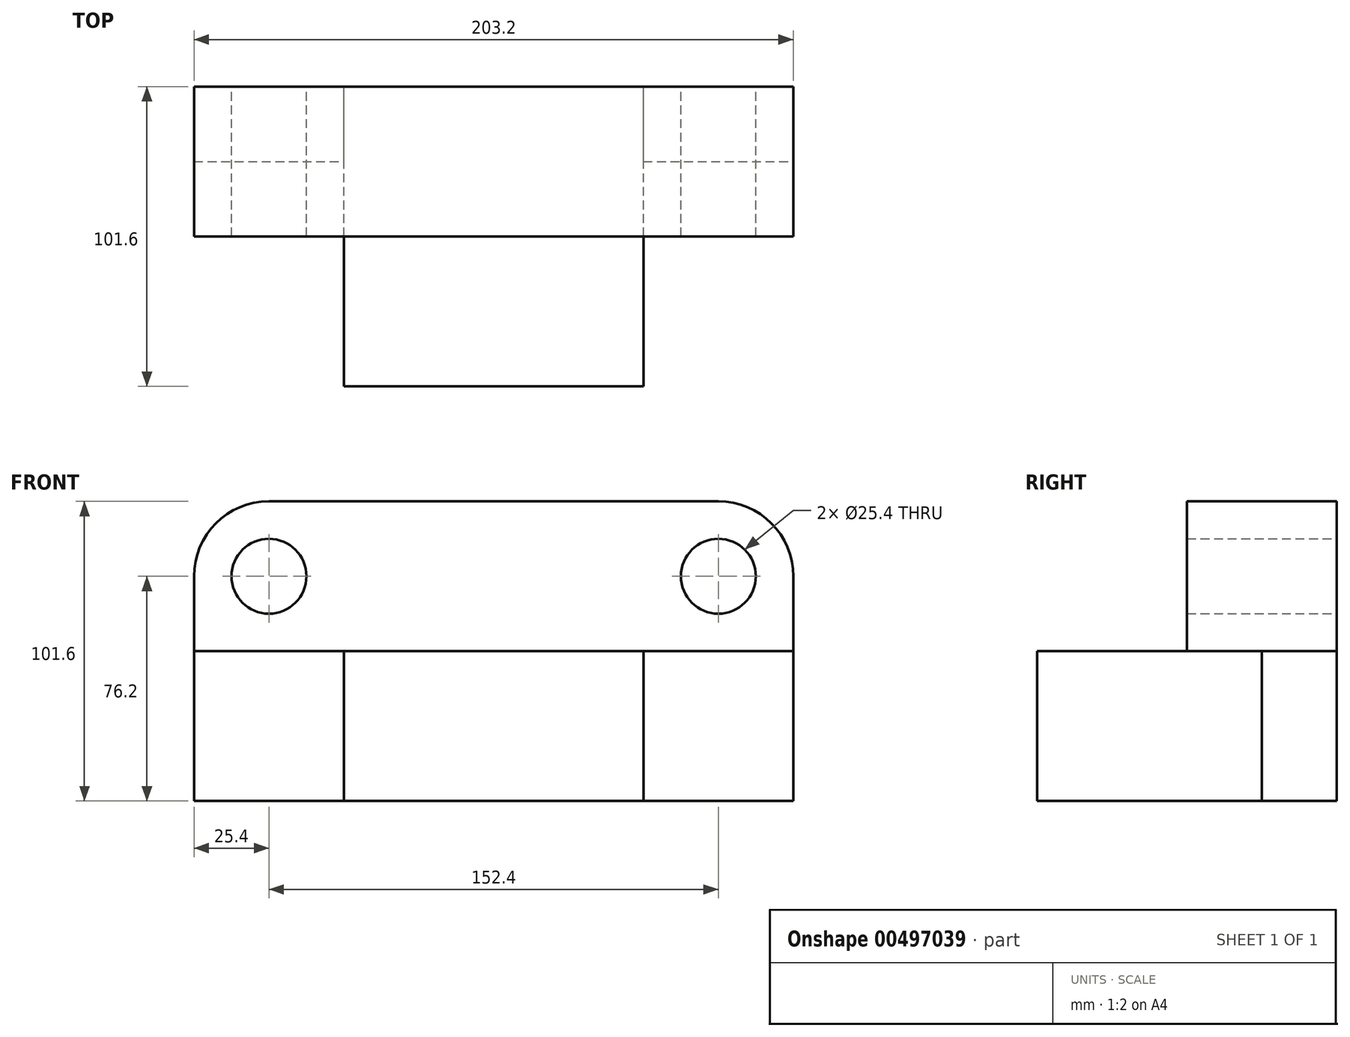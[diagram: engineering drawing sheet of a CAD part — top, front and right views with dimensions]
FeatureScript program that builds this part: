
annotation { "Feature Type Name" : "Feature", "Feature Type Description" : "" }
export const myFeature = defineFeature(function(context is Context, id is Id, definition is map)
    precondition{}
    {
        {
            var Q0;
            Q0=qCreatedBy(makeId("Front.planeOp"),FACE);
            var sketch = newSketch(context, id + "F0", { "sketchPlane" : qUnion([Q0])});
            skLineSegment(sketch, "E0.top", {"start": v(0, 50.8) * mm, "end": v(203.2, 50.8) * mm});
            skLineSegment(sketch, "E1.bottom", {"start": v(0, 0) * mm, "end": v(50.8, 0) * mm});
            skLineSegment(sketch, "E1.left", {"start": v(0, 0) * mm, "end": v(0, 50.8) * mm});
            skLineSegment(sketch, "E1.right", {"start": v(50.8, 0) * mm, "end": v(50.8, 50.8) * mm});
            skLineSegment(sketch, "E2.bottom", {"start": v(50.8, 0) * mm, "end": v(152.4, 0) * mm});
            skLineSegment(sketch, "E2.top", {"start": v(50.8, 50.8) * mm, "end": v(152.4, 50.8) * mm});
            skLineSegment(sketch, "E2.right", {"start": v(152.4, 0) * mm, "end": v(152.4, 50.8) * mm});
            skLineSegment(sketch, "E3.bottom", {"start": v(152.4, 0) * mm, "end": v(203.2, 0) * mm});
            skLineSegment(sketch, "E3.top", {"start": v(152.4, 50.8) * mm, "end": v(203.2, 50.8) * mm});
            skLineSegment(sketch, "E4", {"start": v(203.2, 0) * mm, "end": v(203.2, 50.8) * mm});
            skLineSegment(sketch, "E5.top", {"start": v(0, 101.6) * mm, "end": v(203.2, 101.6) * mm});
            skLineSegment(sketch, "E5.left", {"start": v(0, 50.8) * mm, "end": v(0, 101.6) * mm});
            skLineSegment(sketch, "E5.right", {"start": v(203.2, 50.8) * mm, "end": v(203.2, 101.6) * mm});
            skLineSegment(sketch, "E6", {"start": v(203.2, 101.6) * mm, "end": v(203.2, 76.2) * mm});
            skCircle(sketch, "E7", {"center": v(25.4, 76.2) * mm, "radius": 12.7 * mm});
            skCircle(sketch, "E8", {"center": v(177.8, 76.2) * mm, "radius": 12.7 * mm});
            skLineSegment(sketch, "E9", {"start": v(0, 50.8) * mm, "end": v(50.8, 50.8) * mm});
            skSolve(sketch);
        }
        {
            var Q0;
            Q0=makeQuery(id+"F0.imprint","IMPRINT",FACE,{"disambiguationData":[TD([[makeQuery(id+"F0.imprint","IMPRINT",EDGE,{"derivedFrom":sQuery(id+"F0.wireOp",EDGE,"E1.bottom")}),1.0]])]});
            extrude(context, id + "F1", {"entities" : qUnion([Q0]), "depth" : 25.4 * mm});
        }
        {
            var Q0;
            Q0=makeQuery(id+"F0.imprint","IMPRINT",FACE,{"disambiguationData":[TD([[makeQuery(id+"F0.imprint","IMPRINT",EDGE,{"derivedFrom":sQuery(id+"F0.wireOp",EDGE,"E3.bottom")}),1.0]])]});
            extrude(context, id + "F2", {"entities" : qUnion([Q0]), "depth" : 25.4 * mm});
        }
        {
            var Q0;
            Q0=makeQuery(id+"F0.imprint","IMPRINT",FACE,{"disambiguationData":[TD([[makeQuery(id+"F0.imprint","IMPRINT",EDGE,{"derivedFrom":sQuery(id+"F0.wireOp",EDGE,"E2.bottom")}),1.0]])]});
            extrude(context, id + "F3", {"entities" : qUnion([Q0]), "depth" : 101.6 * mm});
        }
        {
            var Q0;
            Q0=makeQuery(id+"F0.imprint","IMPRINT",FACE,{"disambiguationData":[TD([[makeQuery(id+"F0.imprint","IMPRINT",EDGE,{"derivedFrom":sQuery(id+"F0.wireOp",EDGE,"E5.top")}),-1.0]])]});
            extrude(context, id + "F4", {"entities" : qUnion([Q0]), "depth" : 50.8 * mm});
        }
        {
            var Q0;
            Q0=makeQuery(id+"F4.opExtrude","SWEPT_EDGE",EDGE,{"disambiguationData":[OSD([sQuery(id+"F0.wireOp",EDGE,"E5.top"),sQuery(id+"F0.wireOp",EDGE,"E5.left")])]});
            fillet(context, id + "F5", {"entities" : qUnion([Q0]), "radius" : 25.4 * mm, "tangentPropagation" : true, "allowEdgeOverflow" : false});
        }
        {
            var Q0;
            Q0=makeQuery(id+"F4.opExtrude","SWEPT_EDGE",EDGE,{"disambiguationData":[OSD([sQuery(id+"F0.wireOp",EDGE,"E5.top"),sQuery(id+"F0.wireOp",EDGE,"E5.right")])]});
            fillet(context, id + "F6", {"entities" : qUnion([Q0]), "radius" : 25.4 * mm, "tangentPropagation" : true, "allowEdgeOverflow" : false});
        }
        {
            var Q0;
            Q0=makeQuery(id+"F0.imprint","IMPRINT",FACE,{"disambiguationData":[TD([[makeQuery(id+"F0.imprint","IMPRINT",EDGE,{"derivedFrom":sQuery(id+"F0.wireOp",EDGE,"E8")}),1.0]])]});
            var Q1;
            Q1=makeQuery(id+"F0.imprint","IMPRINT",FACE,{"disambiguationData":[TD([[makeQuery(id+"F0.imprint","IMPRINT",EDGE,{"derivedFrom":sQuery(id+"F0.wireOp",EDGE,"E7")}),1.0]])]});
            extrude(context, id + "F7", {"entities" : qUnion([Q0, Q1]), "operationType" : NewBodyOperationType.REMOVE, "oppositeDirection" : true, "depth" : 25.4 * mm});
        }
    });
